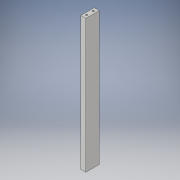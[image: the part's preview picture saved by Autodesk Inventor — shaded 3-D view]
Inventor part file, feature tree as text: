
AUTODESK INVENTOR PART (.ipt)
format: ipt  version: 2017 (Build 210142000, 142)  size: 108,544 bytes
history: native  units: in
note: dims shown in document units (in); Inventor stores cm internally (conversion verified against a paired STEP export)
features: sketch x3, hole x2, extrude x1
ambient origin geometry x8: Origin, YZ Plane, XZ Plane, XY Plane, X Axis, Y Axis, Z Axis, Center Point
bodies: Solid1 (feature_tree)
feature tree (6):
  extrude  "Extrusion1"  Depth=10.0in
  hole  "Hole1"  [1 undecoded]
  hole  "Hole2"  [1 undecoded]
  sketch  "Sketch1"  dims[d0=0.375in d1=10.0in]
  sketch  "Sketch2"  dims[d2=1.0in d3=0.0in]
  sketch  "Sketch3"  dims[d6=0.13in d7=0.25in d8=0.375in d9=0.25in d10=0.5635in d11=0.3in d12=0.8108in d14=0.13in d15=0.25in d16=0.375in d17=0.25in d18=0.5635in d19=0.3in d20=0.8108in]
note: 2 required parameter values undecoded (feature->parameter linkage not recoverable at this tier; creation-order binding heuristic only, values carry confidence <= 0.55)
